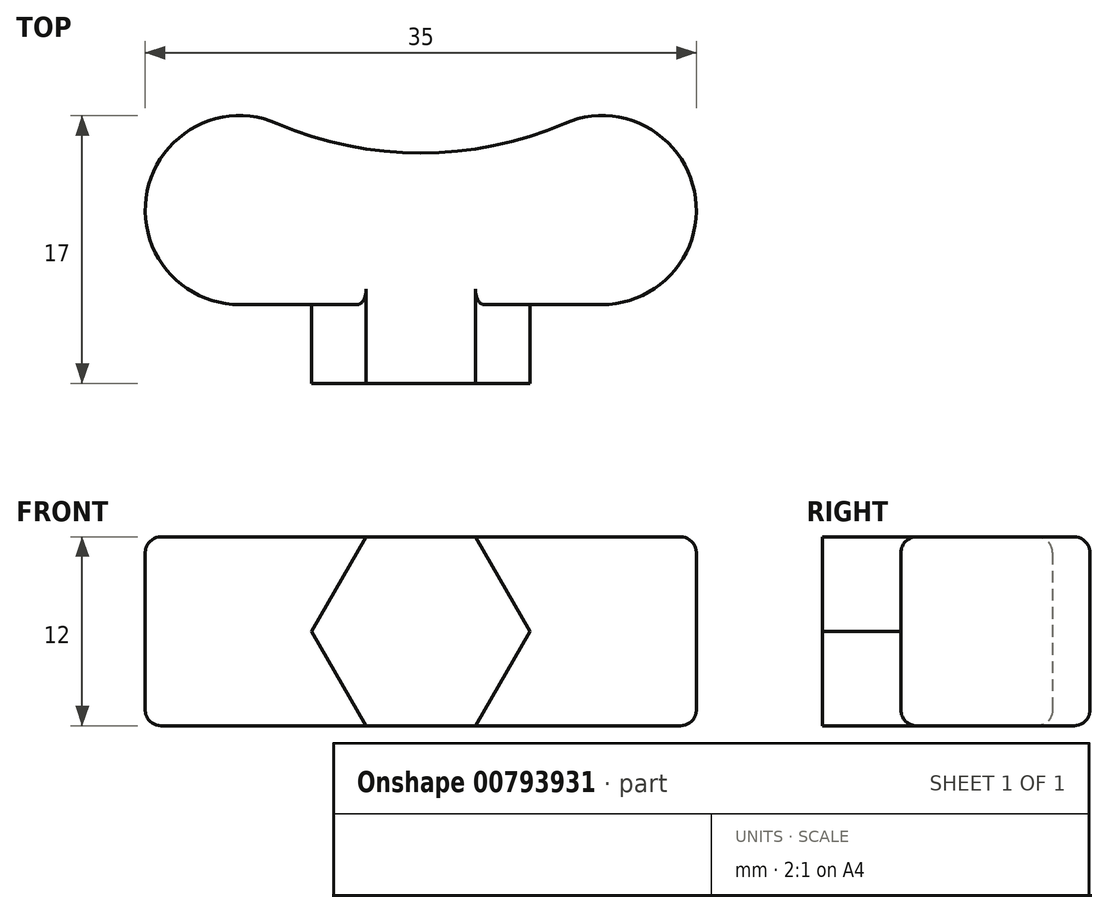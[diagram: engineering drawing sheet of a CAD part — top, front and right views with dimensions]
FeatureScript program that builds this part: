
annotation { "Feature Type Name" : "Feature", "Feature Type Description" : "" }
export const myFeature = defineFeature(function(context is Context, id is Id, definition is map)
    precondition{}
    {
        {
            var Q0;
            Q0=qCreatedBy(makeId("Front.planeOp"),FACE);
            var sketch = newSketch(context, id + "F0", { "sketchPlane" : qUnion([Q0])});
            skCircle(sketch, "E0.cCircle", {"center": v(0, 6) * mm, "radius": 6 * mm, "construction": true});
            skLineSegment(sketch, "E0.0", {"start": v(6.93, 6) * mm, "end": v(3.46, 0) * mm});
            skLineSegment(sketch, "E0.1", {"start": v(3.46, 0) * mm, "end": v(-3.46, 0) * mm});
            skLineSegment(sketch, "E0.2", {"start": v(-3.46, 0) * mm, "end": v(-6.93, 6) * mm});
            skLineSegment(sketch, "E0.3", {"start": v(-6.93, 6) * mm, "end": v(-3.46, 12) * mm});
            skLineSegment(sketch, "E0.4", {"start": v(-3.46, 12) * mm, "end": v(3.46, 12) * mm});
            skLineSegment(sketch, "E0.5", {"start": v(3.46, 12) * mm, "end": v(6.93, 6) * mm});
            skPoint(sketch, "E0.0.midPoint", {"position": v(5.2, 3) * mm});
            skSolve(sketch);
        }
        {
            var Q0;
            Q0=makeQuery(id+"F0.imprint","IMPRINT",FACE,{"disambiguationData":[TD([[makeQuery(id+"F0.imprint","IMPRINT",EDGE,{"derivedFrom":sQuery(id+"F0.wireOp",EDGE,"E0.0")}),-1.0]])]});
            extrude(context, id + "F1", {"entities" : qUnion([Q0]), "depth" : 5 * mm, "offsetDistance" : 25 * mm});
        }
        {
            var Q0;
            Q0=qCreatedBy(makeId("Top.planeOp"),FACE);
            var sketch = newSketch(context, id + "F2", { "sketchPlane" : qUnion([Q0])});
            skLineSegment(sketch, "E1.top", {"start": v(-11.5, 0) * mm, "end": v(11.5, 0) * mm});
            skArc(sketch, "E2", {"start": v(-9.12, 11.5) * mm, "mid": v(-17.38, 7.21) * mm, "end": v(-11.5, 0) * mm});
            skArc(sketch, "E3", {"start": v(11.5, 0) * mm, "mid": v(17.38, 7.21) * mm, "end": v(9.12, 11.5) * mm});
            skArc(sketch, "E4", {"start": v(-9.12, 11.5) * mm, "mid": v(0, 9.62) * mm, "end": v(9.12, 11.5) * mm});
            skPoint(sketch, "E5.orphan", {"position": v(17.5, 0) * mm});
            skSolve(sketch);
        }
        {
            var Q0;
            Q0 = qSketchRegion(id + "F2", true);
            extrude(context, id + "F3", {"entities" : qUnion([Q0]), "operationType" : NewBodyOperationType.ADD, "depth" : 12 * mm, "offsetDistance" : 25 * mm});
        }
        {
            var Q0;
            Q0=makeQuery(id+"F3.opExtrude","CAP_EDGE",EDGE,{"disambiguationData":[OSD([sQuery(id+"F2.wireOp",EDGE,"EAuGkv1U-x0EL-jmG5-r304-wkUbUWQSujRI")])],"isStart":false});
            var Q1;
            Q1=makeQuery(id+"F3.opExtrude","CAP_EDGE",EDGE,{"disambiguationData":[OSD([sQuery(id+"F2.wireOp",EDGE,"EV9zZHbe-cMTm-3Ix2-oie2-m6GrbF1OMPp5")])],"isStart":false});
            var Q2;
            {var subQ1=sQuery(id+"F2.wireOp",EDGE,"E1.top");Q2=makeQuery(id+"F3.boolean.opBoolean","SPLIT",EDGE,{"disambiguationData":[TD([makeQuery(id+"F1.opExtrude","SWEPT_FACE",FACE,{"disambiguationData":[OSD([sQuery(id+"F0.wireOp",EDGE,"E0.5")])]})])],"derivedFrom":makeQuery(id+"F3.opExtrude","CAP_EDGE",EDGE,{"disambiguationData":[OSD([subQ1])],"isStart":false})});}
            var Q3;
            {var subQ1=sQuery(id+"F2.wireOp",EDGE,"E1.top");Q3=makeQuery(id+"F3.boolean.opBoolean","SPLIT",EDGE,{"disambiguationData":[TD([makeQuery(id+"F1.opExtrude","SWEPT_FACE",FACE,{"disambiguationData":[OSD([sQuery(id+"F0.wireOp",EDGE,"E0.0")])]})])],"derivedFrom":makeQuery(id+"F3.opExtrude","CAP_EDGE",EDGE,{"disambiguationData":[OSD([subQ1])],"isStart":true})});}
            var Q4;
            Q4=makeQuery(id+"F3.opExtrude","CAP_EDGE",EDGE,{"disambiguationData":[OSD([sQuery(id+"F2.wireOp",EDGE,"EV9zZHbe-cMTm-3Ix2-oie2-m6GrbF1OMPp5")])],"isStart":true});
            var Q5;
            Q5=makeQuery(id+"F3.opExtrude","CAP_EDGE",EDGE,{"disambiguationData":[OSD([sQuery(id+"F2.wireOp",EDGE,"EAuGkv1U-x0EL-jmG5-r304-wkUbUWQSujRI")])],"isStart":true});
            fillet(context, id + "F4", {"entities" : qUnion([Q0, Q1, Q2, Q3, Q4, Q5]), "radius" : 1 * mm, "tangentPropagation" : true, "allowEdgeOverflow" : false});
        }
    });
